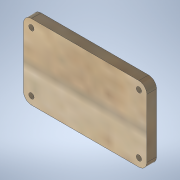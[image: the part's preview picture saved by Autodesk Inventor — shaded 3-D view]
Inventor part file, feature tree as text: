
AUTODESK INVENTOR PART (.ipt)
format: ipt  version: 2020.3 (Build 243373000, 373)  size: 138,240 bytes
history: native  units: mm
features: sketch x3, hole x2, other x1, extrude x1, fillet x1
ambient origin geometry x8: Origin, YZ Plane, XZ Plane, XY Plane, X Axis, Y Axis, Z Axis, Center Point
bodies: Body1 (feature_tree)
feature tree (8):
  other  "ソリッド1"
  extrude  "押し出し1"  Depth=70.0mm
  hole  "穴1"  [1 undecoded]
  fillet  "フィレット1"  Radius=5.5mm
  hole  "穴2"  [1 undecoded]
  sketch  "スケッチ1"
  sketch  "スケッチ2"
  sketch  "スケッチ3"
note: 2 required parameter values undecoded (feature->parameter linkage not recoverable at this tier; creation-order binding heuristic only, values carry confidence <= 0.55)
